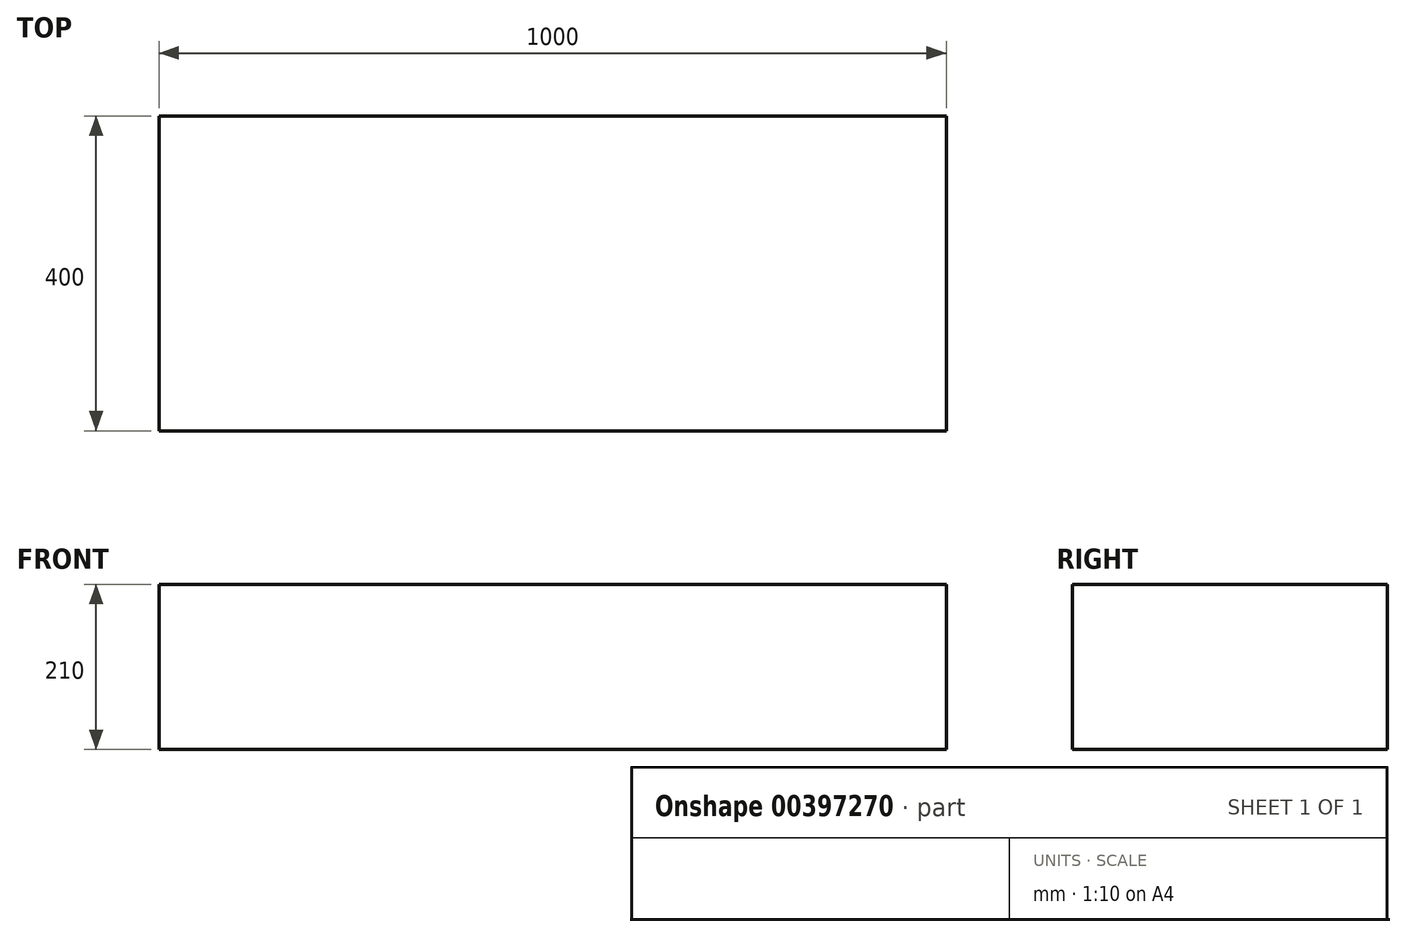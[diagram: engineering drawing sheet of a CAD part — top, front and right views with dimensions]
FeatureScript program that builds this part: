
annotation { "Feature Type Name" : "Feature", "Feature Type Description" : "" }
export const myFeature = defineFeature(function(context is Context, id is Id, definition is map)
    precondition{}
    {
        {
            var Q0;
            Q0=qCreatedBy(makeId("Top.planeOp"),FACE);
            var sketch = newSketch(context, id + "F0", { "sketchPlane" : qUnion([Q0])});
            skLineSegment(sketch, "E0", {"start": v(0, 1110.96) * mm, "end": v(0, -1045.2) * mm, "construction": true});
            skLineSegment(sketch, "E1.bottom", {"start": v(-515.07, 80.82) * mm, "end": v(484.93, 80.82) * mm});
            skLineSegment(sketch, "E1.top", {"start": v(-515.07, -319.18) * mm, "end": v(484.93, -319.18) * mm});
            skLineSegment(sketch, "E1.left", {"start": v(-515.07, 80.82) * mm, "end": v(-515.07, -319.18) * mm});
            skLineSegment(sketch, "E1.right", {"start": v(484.93, 80.82) * mm, "end": v(484.93, -319.18) * mm});
            skSolve(sketch);
        }
        {
            var Q0;
            Q0 = qSketchRegion(id + "F0", true);
            extrude(context, id + "F1", {"entities" : qUnion([Q0]), "depth" : 210 * mm});
        }
    });
